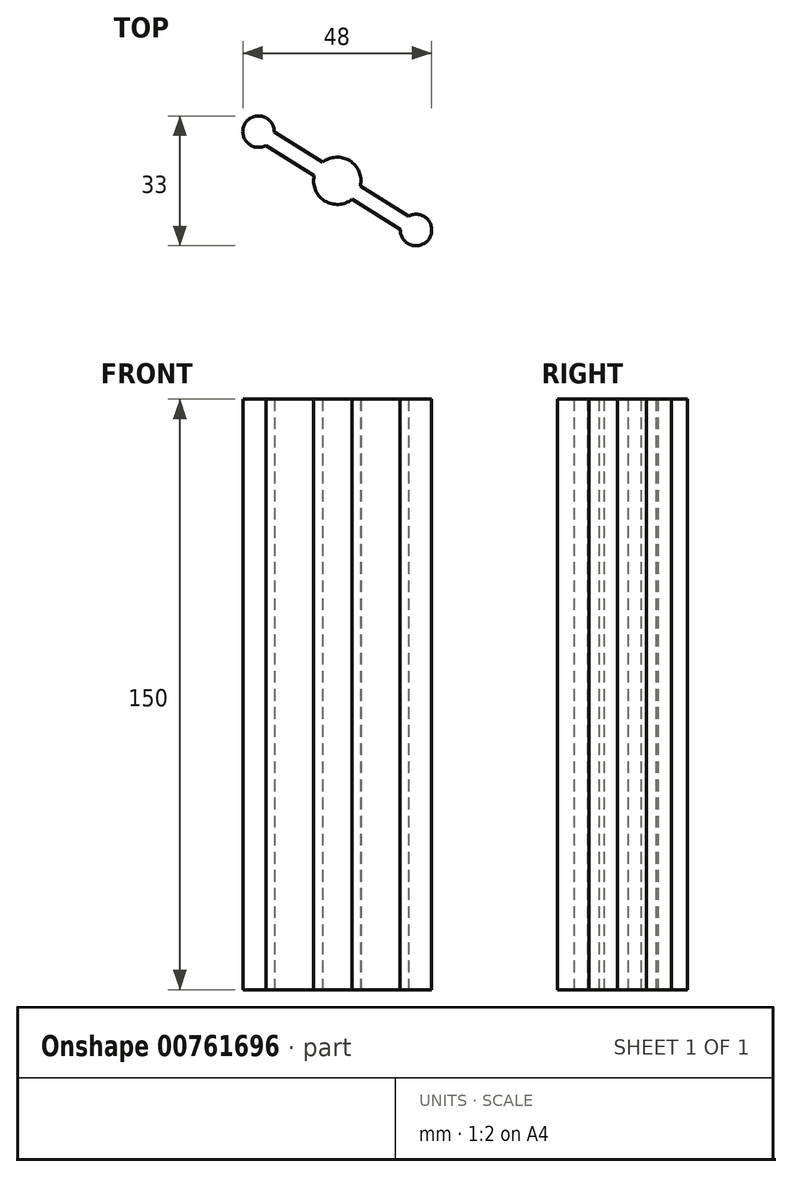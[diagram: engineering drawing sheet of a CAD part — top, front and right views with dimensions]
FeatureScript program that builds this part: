
annotation { "Feature Type Name" : "Feature", "Feature Type Description" : "" }
export const myFeature = defineFeature(function(context is Context, id is Id, definition is map)
    precondition{}
    {
        {
            var Q0;
            Q0=qCreatedBy(makeId("Top.planeOp"),FACE);
            var sketch = newSketch(context, id + "F0", { "sketchPlane" : qUnion([Q0])});
            skPoint(sketch, "E0.middle", {"position": v(0, 0) * mm});
            skArc(sketch, "E1", {"start": v(-16, 12.36) * mm, "mid": v(-23.4, 14.62) * mm, "end": v(-18.12, 8.97) * mm});
            skArc(sketch, "E2", {"start": v(16, -12.36) * mm, "mid": v(23.4, -14.62) * mm, "end": v(18.12, -8.97) * mm});
            skArc(sketch, "E3", {"start": v(-5.86, 1.3) * mm, "mid": v(-3.18, -5.09) * mm, "end": v(3.74, -4.7) * mm});
            skLineSegment(sketch, "E4", {"start": v(23.4, -14.62) * mm, "end": v(-23.4, 14.62) * mm, "construction": true});
            skLineSegment(sketch, "E5.0", {"start": v(16, -12.36) * mm, "end": v(3.74, -4.7) * mm});
            skLineSegment(sketch, "E6.0", {"start": v(18.12, -8.97) * mm, "end": v(5.86, -1.3) * mm});
            skLineSegment(sketch, "E7.trimOffspring", {"start": v(-5.86, 1.3) * mm, "end": v(-18.12, 8.97) * mm});
            skLineSegment(sketch, "E8.trimOffspring", {"start": v(-3.74, 4.7) * mm, "end": v(-16, 12.36) * mm});
            skArc(sketch, "E9.trimOffspring", {"start": v(5.86, -1.3) * mm, "mid": v(3.18, 5.09) * mm, "end": v(-3.74, 4.7) * mm});
            skSolve(sketch);
        }
        {
            var Q0;
            Q0 = qSketchRegion(id + "F0", true);
            extrude(context, id + "F1", {"entities" : qUnion([Q0]), "depth" : 150 * mm, "offsetDistance" : 25 * mm});
        }
    });
